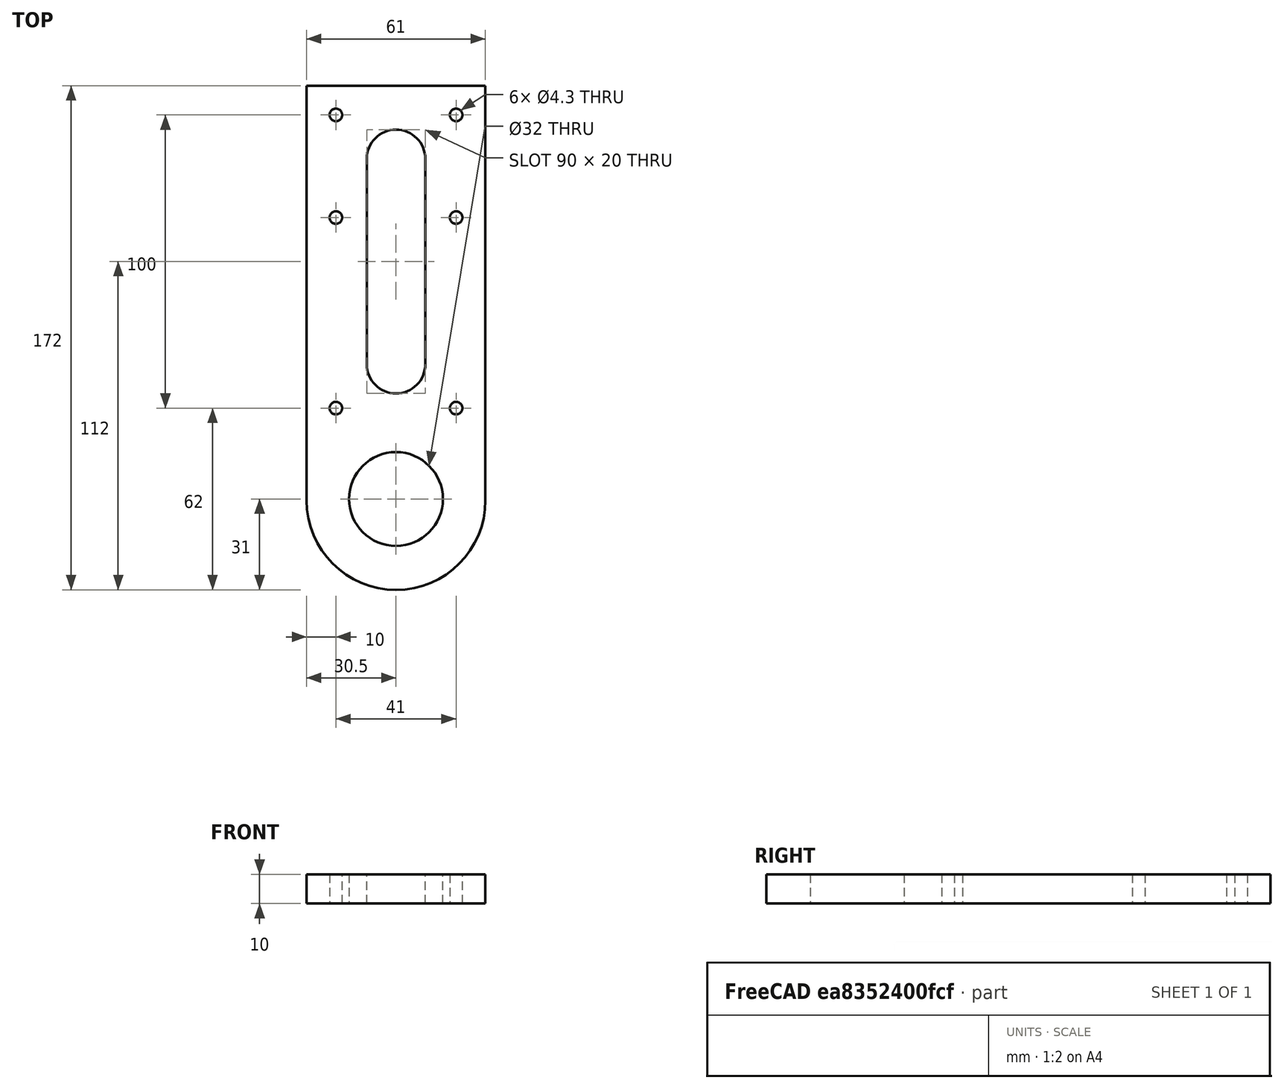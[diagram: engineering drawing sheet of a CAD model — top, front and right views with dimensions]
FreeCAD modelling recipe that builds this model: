
FCSTD DOCUMENT  (FreeCAD 0.22R38127 (Git))
Label: upper2
License: All rights reserved
LicenseURL: http://en.wikipedia.org/wiki/All_rights_reserved
objects: Sketcher::SketchObject×1, PartDesign::Pad×1, PartDesign::Body×1
note: 4 computed .brp shape members not serialized (recipe doc carries the construction recipe); baked Part::Feature solids carry a one-line shape summary decoded from their .brp

FEATURE [Sketcher::SketchObject] Sketch
  AttachmentSupport = -> [XY_Plane]
  FullyConstrained = true
  MapMode = 5
  sketch-geometry (18):
    g0: Circle CenterX=-20.5 CenterY=131 CenterZ=0 NormalX=0 NormalY=0 NormalZ=1 AngleXU=0 Radius=2.15
    g1: Circle CenterX=20.5 CenterY=131 CenterZ=0 NormalX=0 NormalY=0 NormalZ=1 AngleXU=0 Radius=2.15
    g2: Circle CenterX=-20.5 CenterY=96 CenterZ=0 NormalX=0 NormalY=0 NormalZ=1 AngleXU=0 Radius=2.15
    g3: Circle CenterX=20.5 CenterY=96 CenterZ=0 NormalX=0 NormalY=0 NormalZ=1 AngleXU=0 Radius=2.15
    g4: Circle CenterX=0 CenterY=0 CenterZ=0 NormalX=0 NormalY=0 NormalZ=1 AngleXU=0 Radius=16
    g5: GeomPoint X=0 Y=16 Z=0
    g6: Circle CenterX=-20.5 CenterY=31 CenterZ=0 NormalX=0 NormalY=0 NormalZ=1 AngleXU=0 Radius=2.15
    g7: Circle CenterX=20.5 CenterY=31 CenterZ=0 NormalX=0 NormalY=0 NormalZ=1 AngleXU=0 Radius=2.15
    g8: LineSegment StartX=-30.5 StartY=141 StartZ=0 EndX=-30.5 EndY=-0.5 EndZ=0
    g9: LineSegment StartX=30.5 StartY=-0.5 StartZ=0 EndX=30.5 EndY=141 EndZ=0
    g10: LineSegment StartX=30.5 StartY=141 StartZ=0 EndX=-30.5 EndY=141 EndZ=0
    g11: ArcOfCircle CenterX=8e-16 CenterY=-0.5 CenterZ=0 NormalX=0 NormalY=0 NormalZ=1 AngleXU=0 Radius=30.5 StartAngle=3.14159 EndAngle=6.28319
    g12: GeomPoint X=0 Y=-16 Z=0
    g13: GeomPoint X=0 Y=-31 Z=0
    g14: ArcOfCircle CenterX=0 CenterY=116 CenterZ=0 NormalX=0 NormalY=0 NormalZ=1 AngleXU=0 Radius=10 StartAngle=7e-16 EndAngle=3.14159
    g15: ArcOfCircle CenterX=0 CenterY=46 CenterZ=0 NormalX=0 NormalY=0 NormalZ=1 AngleXU=0 Radius=10 StartAngle=3.14159 EndAngle=6.28319
    g16: LineSegment StartX=10 StartY=116 StartZ=0 EndX=10 EndY=46 EndZ=0
    g17: LineSegment StartX=-10 StartY=116 StartZ=0 EndX=-10 EndY=46 EndZ=0
  constraints (43):
    c: Symmetric(g3,g2,g-2)
    c: Symmetric(g0,g1,g-2)
    c: Vertical(g0,g2)
    c: DistanceY(g2,g0) = 35
    c: DistanceX(g0,g1) = 41
    c: PointOnObject(g5,g4)
    c: PointOnObject(g5,g-2)
    c: DistanceY(g5,g2) = 80
    c: Diameter(g4) = 32
    c: Coincident(g4,g-1)
    c: Equal(g0,g2)
    c: Equal(g2,g3)
    c: Equal(g3,g1)
    c: Diameter(g0) = 4.3
    c: Symmetric(g7,g6,g-2)
    c: Vertical(g6,g2)
    c: DistanceY(g5,g6) = 15
    c: Coincident(g9,g10)
    c: Coincident(g10,g8)
    c: Vertical(g8)
    c: DistanceY(g0,g8) = 10
    c: DistanceX(g8,g0) = 10
    c: Symmetric(g8,g9,g-2)
    c: Equal(g6,g2)
    c: Equal(g6,g7)
    c: PointOnObject(g12,g4)
    c: PointOnObject(g12,g-2)
    c: PointOnObject(g13,g11)
    c: PointOnObject(g13,g-2)
    c: DistanceY(g13,g12) = 15
    c: Coincident(g9,g11)
    c: Symmetric(g8,g9,g-2)
    c: Tangent(g8,g11) = -1.5708
    c: Tangent(g14,g16) = 1.5708
    c: Tangent(g14,g17) = -1.5708
    c: Tangent(g15,g16) = 1.5708
    c: Tangent(g15,g17) = -1.5708
    c: Equal(g14,g15)
    c: Vertical(g17)
    c: PointOnObject(g14,g-2)
    c: DistanceY(g6,g15) = 15
    c: DistanceY(g14,g0) = 15
    c: Radius(g14) = 10
FEATURE [PartDesign::Pad] Pad
  Direction = (0,0,1)
  Length = 10
  Length2 = 10
  Profile = -> Sketch
  ReferenceAxis = -> Sketch [N_Axis]
  Refine = true
  Suppressed = false
  Type = 0
FEATURE [PartDesign::Body] Body
  AllowCompound = false
  Group = -> [Sketch,Pad]
  Origin = -> Origin
  Tip = -> Pad
